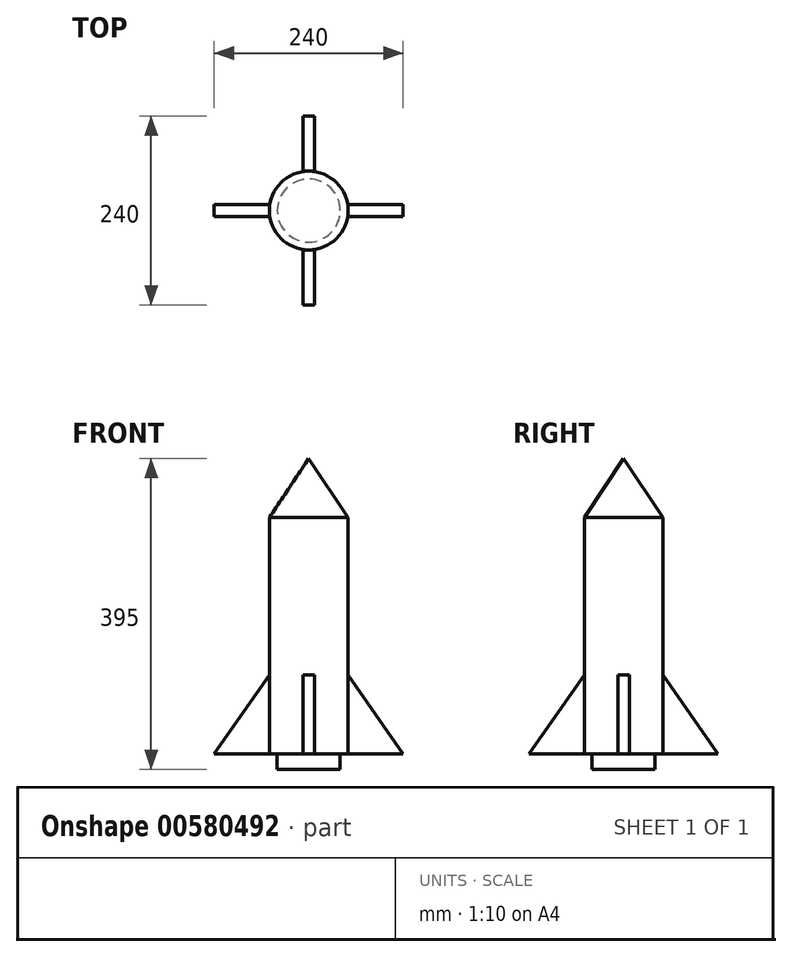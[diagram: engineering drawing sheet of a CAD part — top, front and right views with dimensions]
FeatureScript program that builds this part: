
annotation { "Feature Type Name" : "Feature", "Feature Type Description" : "" }
export const myFeature = defineFeature(function(context is Context, id is Id, definition is map)
    precondition{}
    {
        {
            var Q0;
            Q0=qCreatedBy(makeId("Top.planeOp"),FACE);
            var sketch = newSketch(context, id + "F0", { "sketchPlane" : qUnion([Q0])});
            skCircle(sketch, "E0", {"center": v(0, 0) * mm, "radius": 50 * mm});
            skSolve(sketch);
        }
        {
            var Q0;
            Q0=makeQuery(id+"F0.imprint","IMPRINT",FACE,{"disambiguationData":[TD([[makeQuery(id+"F0.imprint","IMPRINT",EDGE,{"derivedFrom":sQuery(id+"F0.wireOp",EDGE,"E0")}),1.0]])]});
            extrude(context, id + "F1", {"entities" : qUnion([Q0]), "oppositeDirection" : true, "depth" : 300 * mm, "offsetDistance" : 25 * mm});
        }
        {
            var Q0;
            Q0=qCreatedBy(makeId("Front.planeOp"),FACE);
            var sketch = newSketch(context, id + "F2", { "sketchPlane" : qUnion([Q0])});
            skLineSegment(sketch, "E1", {"start": v(0, 0) * mm, "end": v(0, 75) * mm});
            skLineSegment(sketch, "E2", {"start": v(0, 0) * mm, "end": v(50, 0) * mm});
            skLineSegment(sketch, "E3", {"start": v(50, 0) * mm, "end": v(0, 75) * mm});
            skSolve(sketch);
        }
        {
            var Q0;
            Q0=makeQuery(id+"F2.imprint","IMPRINT",FACE,{"disambiguationData":[TD([[makeQuery(id+"F2.imprint","IMPRINT",EDGE,{"derivedFrom":sQuery(id+"F2.wireOp",EDGE,"E1")}),-1.0]])]});
            var Q1;
            Q1=sQuery(id+"F2.wireOp",EDGE,"E1");
            revolve(context, id + "F3", {"operationType" : NewBodyOperationType.ADD, "entities" : qUnion([Q0]), "axis" : qUnion([Q1]), "revolveType" : RevolveType.FULL});
        }
        {
            var Q0;
            Q0=makeQuery(id+"F1.opExtrude","CAP_FACE",FACE,{"disambiguationData":[OSD([sQuery(id+"F0.wireOp",EDGE,"E0")])],"isStart":false});
            var sketch = newSketch(context, id + "F4", { "sketchPlane" : qUnion([Q0])});
            skCircle(sketch, "E4", {"center": v(0, 0) * mm, "radius": 40 * mm});
            skSolve(sketch);
        }
        {
            var Q0;
            Q0=makeQuery(id+"F4.imprint","IMPRINT",FACE,{"disambiguationData":[TD([[makeQuery(id+"F4.imprint","IMPRINT",EDGE,{"derivedFrom":sQuery(id+"F4.wireOp",EDGE,"E4")}),1.0]])]});
            extrude(context, id + "F5", {"entities" : qUnion([Q0]), "operationType" : NewBodyOperationType.ADD, "depth" : 20 * mm, "offsetDistance" : 25 * mm});
        }
        {
            var Q0;
            Q0=qCreatedBy(makeId("Right.planeOp"),FACE);
            var sketch = newSketch(context, id + "F6", { "sketchPlane" : qUnion([Q0])});
            skLineSegment(sketch, "E5", {"start": v(50, 0) * mm, "end": v(50, -300) * mm});
            skLineSegment(sketch, "E6.0", {"start": v(-50, -300) * mm, "end": v(50, -300) * mm});
            skLineSegment(sketch, "E7", {"start": v(40, -300) * mm, "end": v(40, -320) * mm});
            skLineSegment(sketch, "E8", {"start": v(50, -300) * mm, "end": v(120, -300) * mm});
            skLineSegment(sketch, "E9", {"start": v(50, -300) * mm, "end": v(50, -200) * mm});
            skLineSegment(sketch, "E10", {"start": v(50, -200) * mm, "end": v(120, -300) * mm});
            skSolve(sketch);
        }
        {
            var Q0;
            Q0=makeQuery(id+"F6.imprint","IMPRINT",FACE,{"disambiguationData":[TD([[makeQuery(id+"F6.imprint","IMPRINT",EDGE,{"derivedFrom":sQuery(id+"F6.wireOp",EDGE,"E8")}),1.0]])]});
            extrude(context, id + "F7", {"entities" : qUnion([Q0]), "operationType" : NewBodyOperationType.ADD, "endBound" : BoundingType.SYMMETRIC, "depth" : 15 * mm, "offsetDistance" : 25 * mm});
        }
        {
            var Q0;
            Q0=makeQuery(id+"F7.opExtrude","SWEPT_BODY",BODY,{"disambiguationData":[OSD([sQuery(id+"F6.wireOp",EDGE,"E8"),sQuery(id+"F6.wireOp",EDGE,"E9"),sQuery(id+"F6.wireOp",EDGE,"E10")])]});
            var Q1;
            Q1=makeQuery(id+"F3.opRevolve","SWEPT_VERTEX",VERTEX,{"disambiguationData":[OSD([sQuery(id+"F2.wireOp",EDGE,"E1"),sQuery(id+"F2.wireOp",EDGE,"E3")])]});
            var Q2;
            Q2=makeQuery(id+"F1.opExtrude","SWEPT_FACE",FACE,{"disambiguationData":[OSD([sQuery(id+"F0.wireOp",EDGE,"E0")])]});
            transform(context, id + "F8", {"entities" : qUnion([Q0]), "transformType" : TransformType.ROTATION, "transformAxis" : qUnion([Q2]), "angle" : 90 * degree, "makeCopy" : true});
        }
        {
            var Q0;
            Q0=makeQuery(id+"F7.opExtrude","SWEPT_BODY",BODY,{"disambiguationData":[OSD([sQuery(id+"F6.wireOp",EDGE,"E8"),sQuery(id+"F6.wireOp",EDGE,"E9"),sQuery(id+"F6.wireOp",EDGE,"E10")])]});
            var Q1;
            Q1=makeQuery(id+"F1.opExtrude","SWEPT_FACE",FACE,{"disambiguationData":[OSD([sQuery(id+"F0.wireOp",EDGE,"E0")])]});
            transform(context, id + "F9", {"entities" : qUnion([Q0]), "transformType" : TransformType.ROTATION, "transformAxis" : qUnion([Q1]), "angle" : 90 * degree, "oppositeDirection" : true, "makeCopy" : true});
        }
        {
            var Q0;
            Q0=makeQuery(id+"F7.opExtrude","SWEPT_BODY",BODY,{"disambiguationData":[OSD([sQuery(id+"F6.wireOp",EDGE,"E8"),sQuery(id+"F6.wireOp",EDGE,"E9"),sQuery(id+"F6.wireOp",EDGE,"E10")])]});
            var Q1;
            Q1=makeQuery(id+"F1.opExtrude","SWEPT_FACE",FACE,{"disambiguationData":[OSD([sQuery(id+"F0.wireOp",EDGE,"E0")])]});
            transform(context, id + "F10", {"entities" : qUnion([Q0]), "transformType" : TransformType.ROTATION, "transformAxis" : qUnion([Q1]), "angle" : 180 * degree, "makeCopy" : true});
        }
    });
